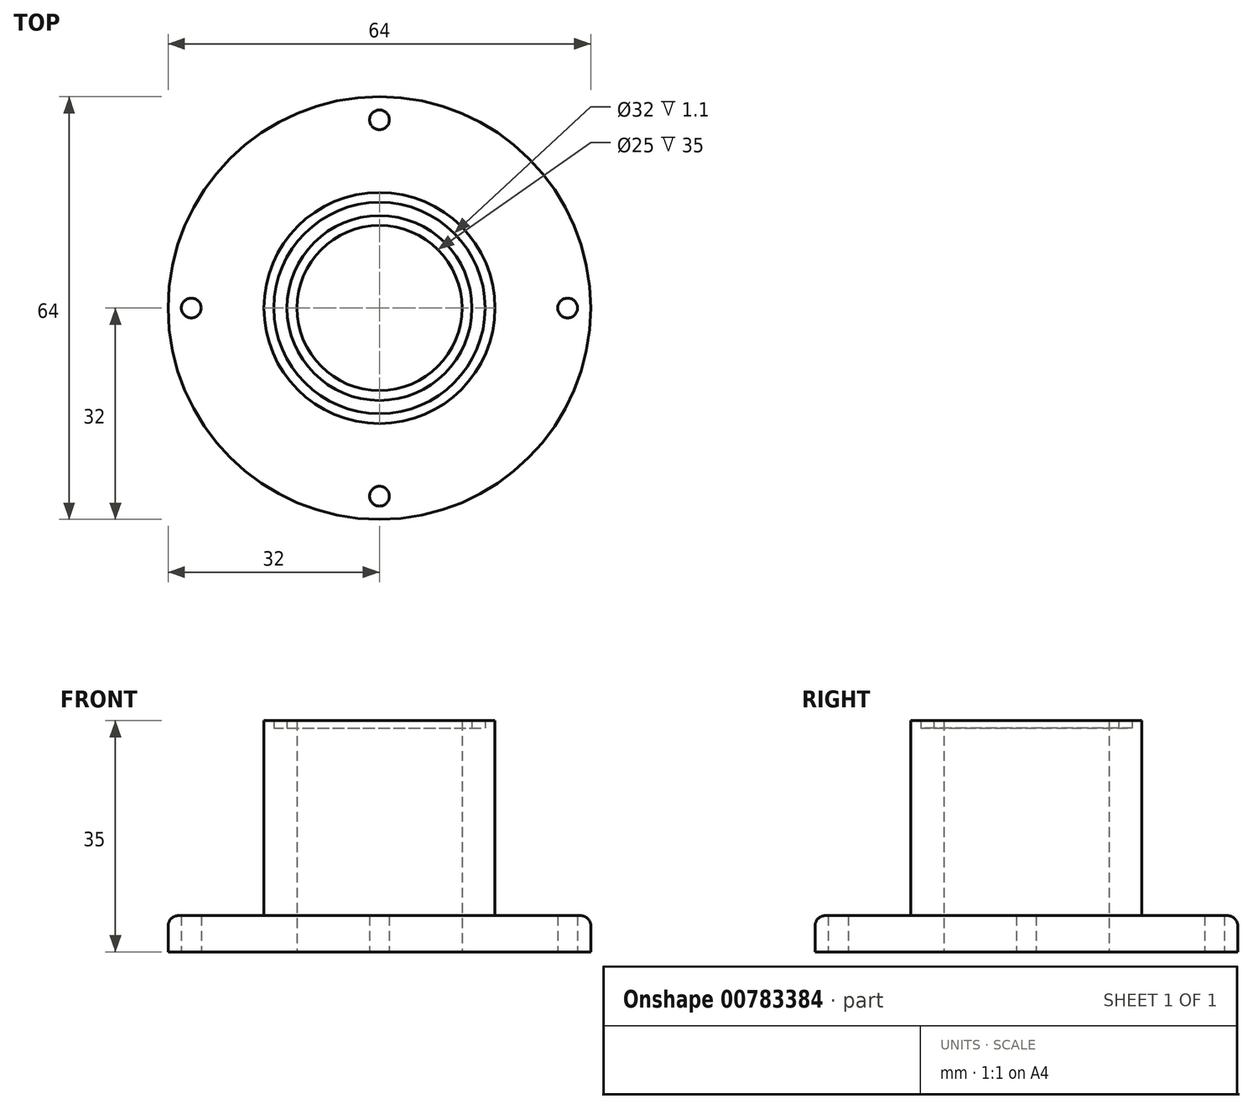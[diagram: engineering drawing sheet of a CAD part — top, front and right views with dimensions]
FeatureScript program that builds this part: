
annotation { "Feature Type Name" : "Feature", "Feature Type Description" : "" }
export const myFeature = defineFeature(function(context is Context, id is Id, definition is map)
    precondition{}
    {
        {
            var Q0;
            Q0=qCreatedBy(makeId("Front.planeOp"),FACE);
            var sketch = newSketch(context, id + "F0", { "sketchPlane" : qUnion([Q0])});
            skLineSegment(sketch, "E0", {"start": v(0, 0) * mm, "end": v(32, 0) * mm});
            skLineSegment(sketch, "E1", {"start": v(0, 5.48) * mm, "end": v(0, 0) * mm});
            skLineSegment(sketch, "E2", {"start": v(0, 0) * mm, "end": v(0, 53.17) * mm});
            skLineSegment(sketch, "E3", {"start": v(32, 0) * mm, "end": v(32, 5.48) * mm});
            skLineSegment(sketch, "E4", {"start": v(32, 5.48) * mm, "end": v(0, 5.48) * mm});
            skLineSegment(sketch, "E5", {"start": v(0, 0) * mm, "end": v(17.5, 0) * mm});
            skLineSegment(sketch, "E6", {"start": v(17.5, 0) * mm, "end": v(17.5, 35) * mm});
            skLineSegment(sketch, "E7", {"start": v(17.5, 35) * mm, "end": v(12.5, 35) * mm});
            skLineSegment(sketch, "E8", {"start": v(12.5, 35) * mm, "end": v(12.5, 0) * mm});
            skLineSegment(sketch, "E9", {"start": v(12.5, 0) * mm, "end": v(17.5, 0) * mm});
            skLineSegment(sketch, "E10", {"start": v(14, 35) * mm, "end": v(14, 33.9) * mm});
            skLineSegment(sketch, "E11", {"start": v(14, 33.9) * mm, "end": v(16, 33.9) * mm});
            skLineSegment(sketch, "E12", {"start": v(16, 33.9) * mm, "end": v(16, 35) * mm});
            skSolve(sketch);
        }
        {
            var Q0;
            {var subQ3=sQuery(id+"F0.wireOp",EDGE,"E3");Q0=makeQuery(id+"F0.imprint","IMPRINT",FACE,{"disambiguationData":[TD([[makeQuery(id+"F0.imprint","IMPRINT",EDGE,{"derivedFrom":subQ3}),1.0]])]});}
            var Q1;
            {var subQ3=sQuery(id+"F0.wireOp",EDGE,"E10");Q1=makeQuery(id+"F0.imprint","IMPRINT",FACE,{"disambiguationData":[TD([[makeQuery(id+"F0.imprint","IMPRINT",EDGE,{"derivedFrom":subQ3}),-1.0]])]});}
            var Q2;
            {var subQ0=sQuery(id+"F0.wireOp",EDGE,"E6");var subQ1=sQuery(id+"F0.wireOp",EDGE,"E0");var subQ2=makeQuery(id+"F0.imprint","INTERSECT",VERTEX,{"derivedFrom":[subQ1,subQ0]});Q2=makeQuery(id+"F0.imprint","IMPRINT",FACE,{"disambiguationData":[TD([[makeQuery(id+"F0.imprint","IMPRINT",EDGE,{"disambiguationData":[TD([[subQ2,1.0]])],"derivedFrom":subQ1}),1.0]])]});}
            var Q3;
            Q3=sQuery(id+"F0.wireOp",EDGE,"E2");
            revolve(context, id + "F1", {"surfaceOperationType" : NewSurfaceOperationType.NEW, "entities" : qUnion([Q0, Q1, Q2]), "axis" : qUnion([Q3]), "revolveType" : RevolveType.FULL});
        }
        {
            var Q0;
            Q0=qCreatedBy(makeId("Top.planeOp"),FACE);
            var sketch = newSketch(context, id + "F2", { "sketchPlane" : qUnion([Q0])});
            skLineSegment(sketch, "E13", {"start": v(0, 0) * mm, "end": v(0, 28.5) * mm});
            skLineSegment(sketch, "E14", {"start": v(0, 0) * mm, "end": v(-28.5, 0) * mm});
            skLineSegment(sketch, "E15", {"start": v(0, 0) * mm, "end": v(28.5, 0) * mm});
            skLineSegment(sketch, "E16", {"start": v(0, 0) * mm, "end": v(0, -28.5) * mm});
            skSolve(sketch);
        }
        {
            var Q0;
            Q0=sQuery(id+"F2.wireOp",VERTEX,"E13.end");
            var Q1;
            Q1=sQuery(id+"F2.wireOp",VERTEX,"E15.end");
            var Q2;
            Q2=sQuery(id+"F2.wireOp",VERTEX,"E16.end");
            var Q3;
            Q3=sQuery(id+"F2.wireOp",VERTEX,"E14.end");
            var Q4;
            Q4=makeQuery(id+"F1.opRevolve","SWEPT_BODY",BODY,{"disambiguationData":[OSD([sQuery(id+"F0.wireOp",EDGE,"E0"),sQuery(id+"F0.wireOp",EDGE,"E3"),sQuery(id+"F0.wireOp",EDGE,"E4"),sQuery(id+"F0.wireOp",EDGE,"E6"),sQuery(id+"F0.wireOp",EDGE,"E7"),sQuery(id+"F0.wireOp",EDGE,"E8"),sQuery(id+"F0.wireOp",EDGE,"E10"),sQuery(id+"F0.wireOp",EDGE,"E11"),sQuery(id+"F0.wireOp",EDGE,"E12")])]});
            hole(context, id + "F3", {"style" : HoleStyle.SIMPLE, "endStyle" : HoleEndStyle.THROUGH, "oppositeDirection" : true, "holeDiameter" : 3 * mm, "majorDiameter" : 5 * mm, "isTappedThrough" : true, "tappedDepth" : 12 * mm, "tapClearance" : 3, "locations" : qUnion([Q0, Q1, Q2, Q3]), "scope" : qUnion([Q4])});
        }
        {
            var Q0;
            Q0=makeQuery(id+"F1.opRevolve","SWEPT_EDGE",EDGE,{"disambiguationData":[OSD([sQuery(id+"F0.wireOp",EDGE,"E3"),sQuery(id+"F0.wireOp",EDGE,"E4")])]});
            fillet(context, id + "F4", {"entities" : qUnion([Q0]), "radius" : 1.5 * mm, "tangentPropagation" : true, "allowEdgeOverflow" : false});
        }
    });
